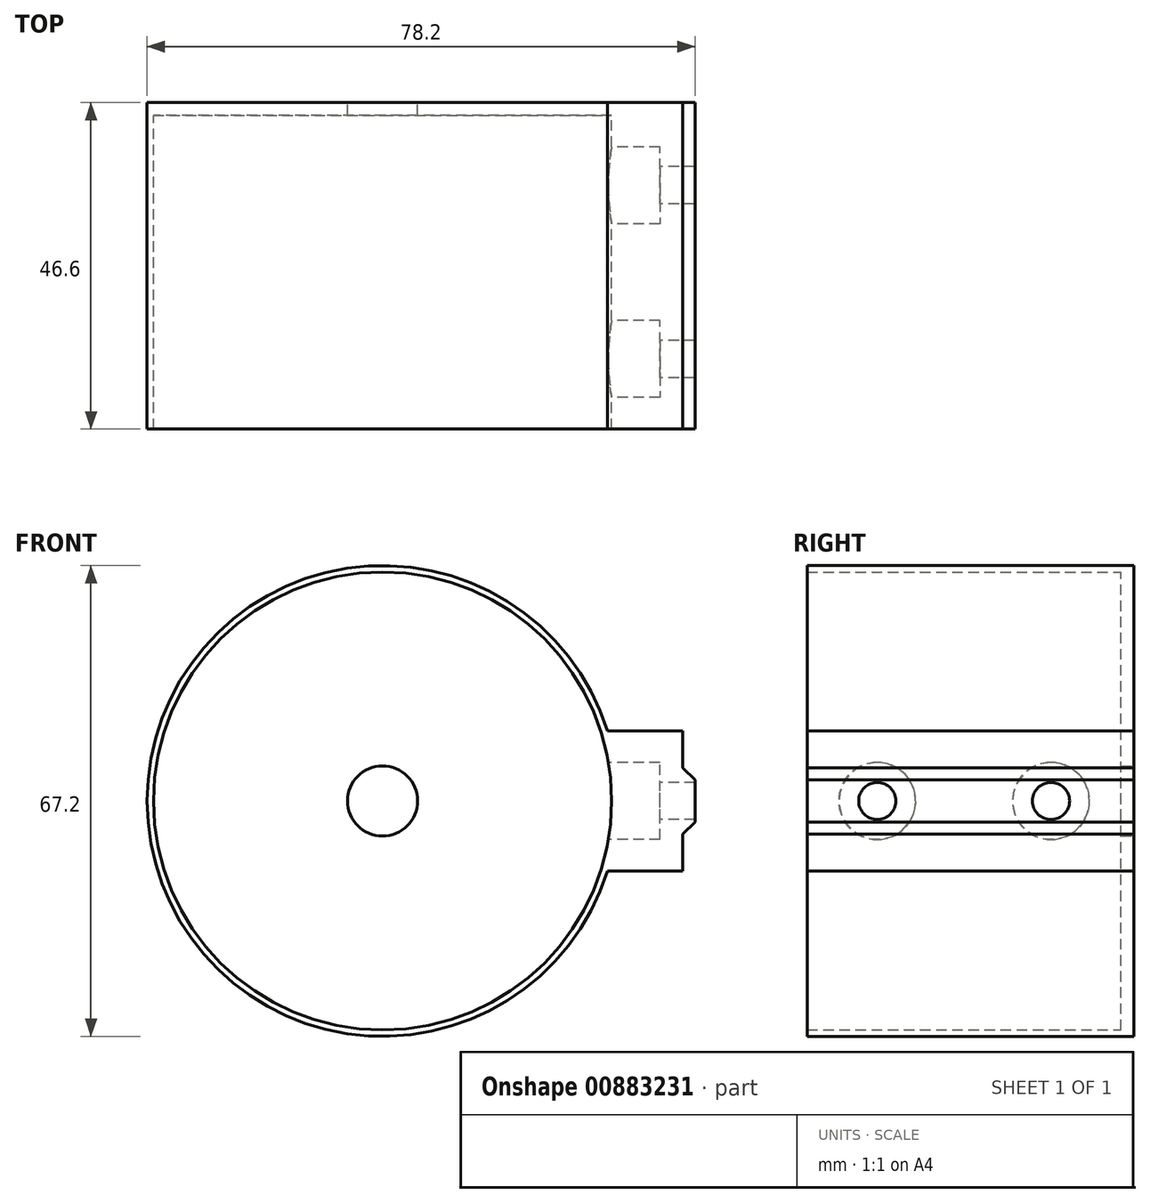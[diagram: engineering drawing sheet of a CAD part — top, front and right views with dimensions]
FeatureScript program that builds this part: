
annotation { "Feature Type Name" : "Feature", "Feature Type Description" : "" }
export const myFeature = defineFeature(function(context is Context, id is Id, definition is map)
    precondition{}
    {
        {
            var Q0;
            Q0=qCreatedBy(makeId("Front.planeOp"),FACE);
            var sketch = newSketch(context, id + "F0", { "sketchPlane" : qUnion([Q0])});
            skCircle(sketch, "E0", {"center": v(0, 0) * mm, "radius": 33.6 * mm});
            skCircle(sketch, "E1", {"center": v(0, 0) * mm, "radius": 32.7 * mm});
            skLineSegment(sketch, "E2", {"start": v(32.08, 10) * mm, "end": v(42.85, 10) * mm});
            skLineSegment(sketch, "E3", {"start": v(42.85, 10) * mm, "end": v(42.85, -10) * mm});
            skLineSegment(sketch, "E4", {"start": v(42.85, -10) * mm, "end": v(32.08, -10) * mm});
            skLineSegment(sketch, "E5", {"start": v(33.6, 0) * mm, "end": v(42.85, 0) * mm});
            skPoint(sketch, "E5.startSnap0", {"position": v(42.85, 0) * mm});
            skLineSegment(sketch, "E6", {"start": v(42.85, 4.75) * mm, "end": v(44.6, 3) * mm});
            skLineSegment(sketch, "E7", {"start": v(44.6, 3) * mm, "end": v(44.6, -3) * mm});
            skLineSegment(sketch, "E8", {"start": v(44.6, -3) * mm, "end": v(42.85, -4.75) * mm});
            skSolve(sketch);
        }
        {
            var Q0;
            Q0=qCreatedBy(makeId("Front.planeOp"),FACE);
            var sketch = newSketch(context, id + "F1", { "sketchPlane" : qUnion([Q0])});
            skCircle(sketch, "E9", {"center": v(0, 0) * mm, "radius": 32.7 * mm});
            skCircle(sketch, "E10", {"center": v(0, 0) * mm, "radius": 5 * mm});
            skSolve(sketch);
        }
        {
            var Q0;
            Q0 = qSketchRegion(id + "F1", true);
            extrude(context, id + "F2", {"entities" : qUnion([Q0]), "depth" : 1.8 * mm, "offsetDistance" : 25 * mm});
        }
        {
            var Q0;
            Q0 = qSketchRegion(id + "F0", true);
            extrude(context, id + "F3", {"entities" : qUnion([Q0]), "operationType" : NewBodyOperationType.ADD, "depth" : 46.6 * mm, "offsetDistance" : 25 * mm});
        }
        {
            var Q0;
            Q0=qCreatedBy(makeId("Right.planeOp"),FACE);
            var sketch = newSketch(context, id + "F4", { "sketchPlane" : qUnion([Q0])});
            skCircle(sketch, "E11", {"center": v(-11.8, 0) * mm, "radius": 2.65 * mm});
            skCircle(sketch, "E12", {"center": v(-36.6, 0) * mm, "radius": 2.65 * mm});
            skSolve(sketch);
        }
        {
            var Q0;
            Q0 = qSketchRegion(id + "F4", true);
            extrude(context, id + "F5", {"entities" : qUnion([Q0]), "operationType" : NewBodyOperationType.REMOVE, "endBound" : BoundingType.THROUGH_ALL, "depth" : 25 * mm, "offsetDistance" : 25 * mm});
        }
        {
            var Q0;
            Q0=qCreatedBy(makeId("Right.planeOp"),FACE);
            var sketch = newSketch(context, id + "F6", { "sketchPlane" : qUnion([Q0])});
            skCircle(sketch, "E13", {"center": v(-11.8, 0) * mm, "radius": 5.5 * mm});
            skCircle(sketch, "E14", {"center": v(-36.6, 0) * mm, "radius": 5.5 * mm});
            skSolve(sketch);
        }
        {
            var Q0;
            Q0 = qSketchRegion(id + "F6", true);
            extrude(context, id + "F7", {"entities" : qUnion([Q0]), "operationType" : NewBodyOperationType.REMOVE, "depth" : 39.6 * mm, "offsetDistance" : 25 * mm});
        }
    });
